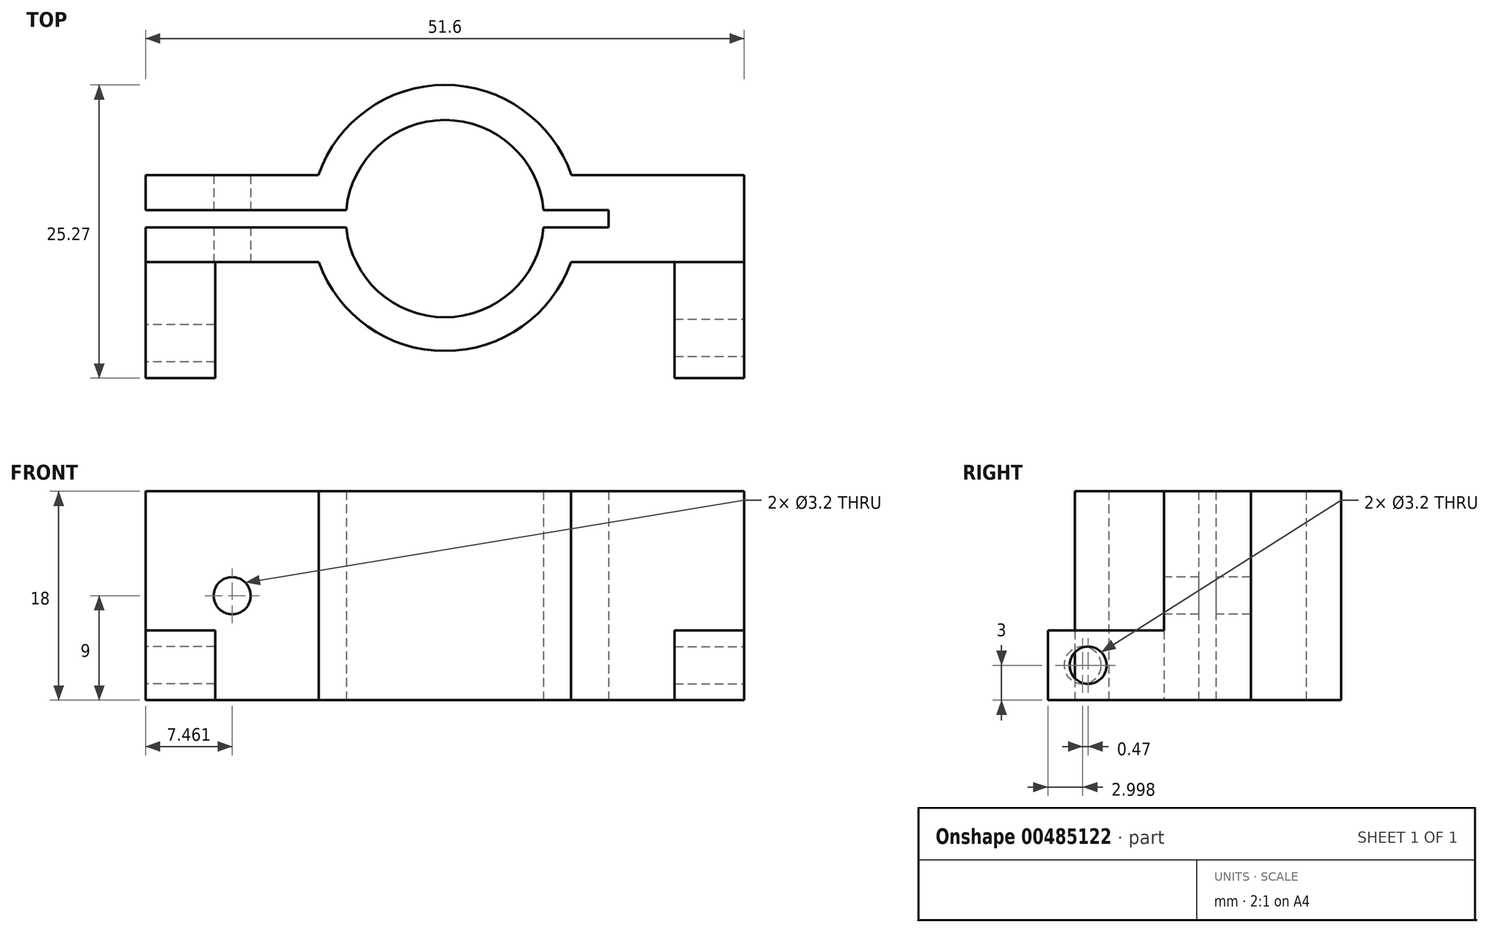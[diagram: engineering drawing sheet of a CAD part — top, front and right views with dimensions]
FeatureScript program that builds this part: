
annotation { "Feature Type Name" : "Feature", "Feature Type Description" : "" }
export const myFeature = defineFeature(function(context is Context, id is Id, definition is map)
    precondition{}
    {
        {
            var Q0;
            Q0=qCreatedBy(makeId("Top.planeOp"),FACE);
            var sketch = newSketch(context, id + "F0", { "sketchPlane" : qUnion([Q0])});
            skLineSegment(sketch, "E0.bottom", {"start": v(-14.3, 13.28) * mm, "end": v(3, 13.28) * mm, "construction": true});
            skLineSegment(sketch, "E0.left", {"start": v(-14.3, 13.28) * mm, "end": v(-14.3, 10.28) * mm, "construction": true});
            skLineSegment(sketch, "E0.right", {"start": v(3, 13.28) * mm, "end": v(3, 10.28) * mm, "construction": true});
            skLineSegment(sketch, "E1.bottom", {"start": v(20, 10.28) * mm, "end": v(37.3, 10.28) * mm, "construction": true});
            skLineSegment(sketch, "E1.top", {"start": v(20, 13.28) * mm, "end": v(33.6, 13.28) * mm, "construction": true});
            skLineSegment(sketch, "E1.left", {"start": v(20, 10.28) * mm, "end": v(20, 13.28) * mm, "construction": true});
            skLineSegment(sketch, "E2", {"start": v(0, 13.28) * mm, "end": v(0, 10.28) * mm, "construction": true});
            skLineSegment(sketch, "E3", {"start": v(23, 13.28) * mm, "end": v(23, 10.28) * mm, "construction": true});
            skLineSegment(sketch, "E4", {"start": v(-14.3, 13.28) * mm, "end": v(3, 13.28) * mm});
            skLineSegment(sketch, "E5", {"start": v(20, 13.28) * mm, "end": v(23, 13.28) * mm});
            skLineSegment(sketch, "E6", {"start": v(20, 13.28) * mm, "end": v(20, 10.28) * mm});
            skLineSegment(sketch, "E7", {"start": v(3, 13.28) * mm, "end": v(3, 10.28) * mm});
            skLineSegment(sketch, "E8", {"start": v(-14.3, 13.28) * mm, "end": v(-14.3, 10.28) * mm});
            skLineSegment(sketch, "E9", {"start": v(37.3, 10.28) * mm, "end": v(23, 10.28) * mm});
            skLineSegment(sketch, "E10.bottom", {"start": v(33.6, 14.78) * mm, "end": v(20, 14.78) * mm, "construction": true});
            skLineSegment(sketch, "E10.top", {"start": v(37.3, 17.78) * mm, "end": v(20, 17.78) * mm, "construction": true});
            skLineSegment(sketch, "E10.right", {"start": v(20, 14.78) * mm, "end": v(20, 17.78) * mm, "construction": true});
            skLineSegment(sketch, "E11", {"start": v(23, 13.28) * mm, "end": v(23, 17.78) * mm, "construction": true});
            skLineSegment(sketch, "E12.bottom", {"start": v(3, 14.78) * mm, "end": v(-14.3, 14.78) * mm, "construction": true});
            skLineSegment(sketch, "E12.top", {"start": v(3, 17.78) * mm, "end": v(-14.3, 17.78) * mm, "construction": true});
            skLineSegment(sketch, "E12.left", {"start": v(3, 14.78) * mm, "end": v(3, 17.78) * mm, "construction": true});
            skLineSegment(sketch, "E12.right", {"start": v(-14.3, 14.78) * mm, "end": v(-14.3, 17.78) * mm, "construction": true});
            skLineSegment(sketch, "E13", {"start": v(20, 14.78) * mm, "end": v(20, 13.28) * mm, "construction": true});
            skPoint(sketch, "E14", {"position": v(20, 14.03) * mm});
            skLineSegment(sketch, "E15", {"start": v(3, 14.78) * mm, "end": v(3, 13.28) * mm, "construction": true});
            skLineSegment(sketch, "E16", {"start": v(3, 14.03) * mm, "end": v(20, 14.03) * mm, "construction": true});
            skPoint(sketch, "E17", {"position": v(11.5, 14.03) * mm});
            skArc(sketch, "E18", {"start": v(20, 14.78) * mm, "mid": v(11.5, 22.54) * mm, "end": v(3, 14.78) * mm, "construction": true});
            skArc(sketch, "E19", {"start": v(3, 13.28) * mm, "mid": v(11.5, 5.48) * mm, "end": v(20, 13.28) * mm, "construction": true});
            skArc(sketch, "E20", {"start": v(0, 13.28) * mm, "mid": v(11.5, 2.57) * mm, "end": v(23, 13.28) * mm, "construction": true});
            skArc(sketch, "E21", {"start": v(23, 14.78) * mm, "mid": v(11.5, 25.58) * mm, "end": v(0, 14.78) * mm, "construction": true});
            skLineSegment(sketch, "E22", {"start": v(25.6, 14.78) * mm, "end": v(25.6, 13.28) * mm, "construction": true});
            skLineSegment(sketch, "E23", {"start": v(-14.3, 10.28) * mm, "end": v(3, 10.28) * mm, "construction": true});
            skLineSegment(sketch, "E24", {"start": v(-14.3, 10.28) * mm, "end": v(0.62, 10.28) * mm});
            skLineSegment(sketch, "E25", {"start": v(-14.3, 14.78) * mm, "end": v(3, 14.78) * mm});
            skLineSegment(sketch, "E26", {"start": v(-14.3, 14.78) * mm, "end": v(-14.3, 17.78) * mm});
            skLineSegment(sketch, "E27", {"start": v(-14.3, 17.78) * mm, "end": v(0.6, 17.78) * mm});
            skLineSegment(sketch, "E28", {"start": v(20, 13.28) * mm, "end": v(25.6, 13.28) * mm});
            skLineSegment(sketch, "E29", {"start": v(25.6, 13.28) * mm, "end": v(25.6, 14.78) * mm});
            skLineSegment(sketch, "E30", {"start": v(25.6, 14.78) * mm, "end": v(20, 14.78) * mm});
            skLineSegment(sketch, "E31", {"start": v(37.3, 17.78) * mm, "end": v(22.4, 17.78) * mm});
            skArc(sketch, "E32", {"start": v(20, 14.78) * mm, "mid": v(11.5, 22.53) * mm, "end": v(3, 14.78) * mm});
            skArc(sketch, "E33", {"start": v(3, 13.28) * mm, "mid": v(11.5, 5.52) * mm, "end": v(20, 13.28) * mm});
            skArc(sketch, "E34", {"start": v(0.62, 10.28) * mm, "mid": v(11.5, 2.62) * mm, "end": v(22.38, 10.28) * mm});
            skArc(sketch, "E35", {"start": v(22.4, 17.78) * mm, "mid": v(11.5, 25.55) * mm, "end": v(0.6, 17.78) * mm});
            skLineSegment(sketch, "E36", {"start": v(37.3, 17.78) * mm, "end": v(37.3, 10.28) * mm});
            skLineSegment(sketch, "E37", {"start": v(23, 10.28) * mm, "end": v(22.38, 10.28) * mm});
            skSolve(sketch);
        }
        {
            var Q0;
            Q0 = qSketchRegion(id + "F0", true);
            extrude(context, id + "F1", {"entities" : qUnion([Q0]), "depth" : 18 * mm, "offsetDistance" : 25 * mm});
        }
        {
            var Q0;
            Q0=makeQuery(id+"F1.opExtrude","SWEPT_FACE",FACE,{"disambiguationData":[OSD([sQuery(id+"F0.wireOp",EDGE,"E24")])]});
            var sketch = newSketch(context, id + "F2", { "sketchPlane" : qUnion([Q0])});
            skLineSegment(sketch, "E38.bottom", {"start": v(-14.3, 18) * mm, "end": v(0.62, 18) * mm, "construction": true});
            skLineSegment(sketch, "E38.top", {"start": v(-14.3, 0) * mm, "end": v(0.62, 0) * mm, "construction": true});
            skLineSegment(sketch, "E38.left", {"start": v(-14.3, 18) * mm, "end": v(-14.3, 0) * mm, "construction": true});
            skLineSegment(sketch, "E38.right", {"start": v(0.62, 18) * mm, "end": v(0.62, 0) * mm, "construction": true});
            skLineSegment(sketch, "E39", {"start": v(-6.84, 18) * mm, "end": v(-6.84, 0) * mm, "construction": true});
            skLineSegment(sketch, "E40", {"start": v(-14.3, 9) * mm, "end": v(0.62, 9) * mm, "construction": true});
            skCircle(sketch, "E41", {"center": v(-6.84, 9) * mm, "radius": 0.84 * mm, "construction": true});
            skSolve(sketch);
        }
        {
            var Q0;
            Q0=sQuery(id+"F2.wireOp",VERTEX,"E41.center");
            var Q1;
            Q1=makeQuery(id+"F1.opExtrude","SWEPT_BODY",BODY,{"disambiguationData":[OSD([sQuery(id+"F0.wireOp",EDGE,"E4"),sQuery(id+"F0.wireOp",EDGE,"E8"),sQuery(id+"F0.wireOp",EDGE,"E9"),sQuery(id+"F0.wireOp",EDGE,"E24"),sQuery(id+"F0.wireOp",EDGE,"E25"),sQuery(id+"F0.wireOp",EDGE,"E26"),sQuery(id+"F0.wireOp",EDGE,"E27"),sQuery(id+"F0.wireOp",EDGE,"E28"),sQuery(id+"F0.wireOp",EDGE,"E29"),sQuery(id+"F0.wireOp",EDGE,"E30"),sQuery(id+"F0.wireOp",EDGE,"E31"),sQuery(id+"F0.wireOp",EDGE,"E32"),sQuery(id+"F0.wireOp",EDGE,"E33"),sQuery(id+"F0.wireOp",EDGE,"E34"),sQuery(id+"F0.wireOp",EDGE,"E35"),sQuery(id+"F0.wireOp",EDGE,"E36"),sQuery(id+"F0.wireOp",EDGE,"E37")])]});
            hole(context, id + "F3", {"style" : HoleStyle.SIMPLE, "endStyle" : HoleEndStyle.BLIND, "holeDiameter" : 3.2 * mm, "holeDepth" : 15 * mm, "isTappedThrough" : true, "tappedDepth" : 12 * mm, "tapClearance" : 3, "locations" : qUnion([Q0]), "scope" : qUnion([Q1])});
        }
        {
            var Q0;
            Q0=makeQuery(id+"F1.opExtrude","SWEPT_FACE",FACE,{"disambiguationData":[OSD([sQuery(id+"F0.wireOp",EDGE,"E9"),sQuery(id+"F0.wireOp",EDGE,"E37")])]});
            var sketch = newSketch(context, id + "F4", { "sketchPlane" : qUnion([Q0])});
            skLineSegment(sketch, "E42.bottom", {"start": v(22.38, 0) * mm, "end": v(37.3, 0) * mm, "construction": true});
            skLineSegment(sketch, "E42.top", {"start": v(22.38, 6) * mm, "end": v(37.3, 6) * mm, "construction": true});
            skLineSegment(sketch, "E42.left", {"start": v(22.38, 0) * mm, "end": v(22.38, 6) * mm, "construction": true});
            skLineSegment(sketch, "E42.right", {"start": v(37.3, 0) * mm, "end": v(37.3, 6) * mm, "construction": true});
            skLineSegment(sketch, "E43", {"start": v(31.3, 6) * mm, "end": v(31.3, 0) * mm, "construction": true});
            skLineSegment(sketch, "E44.bottom", {"start": v(31.3, 6) * mm, "end": v(37.3, 6) * mm});
            skLineSegment(sketch, "E44.top", {"start": v(31.3, 0) * mm, "end": v(37.3, 0) * mm});
            skLineSegment(sketch, "E44.left", {"start": v(31.3, 6) * mm, "end": v(31.3, 0) * mm});
            skLineSegment(sketch, "E44.right", {"start": v(37.3, 6) * mm, "end": v(37.3, 0) * mm});
            skSolve(sketch);
        }
        {
            var Q0;
            Q0=makeQuery(id+"F4.imprint","IMPRINT",FACE,{"disambiguationData":[TD([[makeQuery(id+"F4.imprint","IMPRINT",EDGE,{"derivedFrom":sQuery(id+"F4.wireOp",EDGE,"E44.bottom")}),-1.0]])]});
            extrude(context, id + "F5", {"entities" : qUnion([Q0]), "operationType" : NewBodyOperationType.ADD, "depth" : 10 * mm, "offsetDistance" : 25 * mm});
        }
        {
            var Q0;
            Q0=makeQuery(id+"F1.opExtrude","SWEPT_FACE",FACE,{"disambiguationData":[OSD([sQuery(id+"F0.wireOp",EDGE,"E24")])]});
            var sketch = newSketch(context, id + "F6", { "sketchPlane" : qUnion([Q0])});
            skLineSegment(sketch, "E45.bottom", {"start": v(-14.3, 0) * mm, "end": v(0.62, 0) * mm, "construction": true});
            skLineSegment(sketch, "E45.top", {"start": v(-14.3, 6) * mm, "end": v(0.62, 6) * mm, "construction": true});
            skLineSegment(sketch, "E45.left", {"start": v(-14.3, 0) * mm, "end": v(-14.3, 6) * mm, "construction": true});
            skLineSegment(sketch, "E45.right", {"start": v(0.62, 0) * mm, "end": v(0.62, 6) * mm, "construction": true});
            skLineSegment(sketch, "E46", {"start": v(-8.3, 6) * mm, "end": v(-8.3, 0) * mm, "construction": true});
            skLineSegment(sketch, "E47.bottom", {"start": v(-14.3, 6) * mm, "end": v(-8.3, 6) * mm});
            skLineSegment(sketch, "E47.top", {"start": v(-14.3, 0) * mm, "end": v(-8.3, 0) * mm});
            skLineSegment(sketch, "E47.left", {"start": v(-14.3, 6) * mm, "end": v(-14.3, 0) * mm});
            skLineSegment(sketch, "E47.right", {"start": v(-8.3, 6) * mm, "end": v(-8.3, 0) * mm});
            skSolve(sketch);
        }
        {
            var Q0;
            Q0=makeQuery(id+"F6.imprint","IMPRINT",FACE,{"disambiguationData":[TD([[makeQuery(id+"F6.imprint","IMPRINT",EDGE,{"derivedFrom":sQuery(id+"F6.wireOp",EDGE,"E47.bottom")}),-1.0]])]});
            extrude(context, id + "F7", {"entities" : qUnion([Q0]), "operationType" : NewBodyOperationType.ADD, "depth" : 10 * mm, "offsetDistance" : 25 * mm});
        }
        {
            var Q0;
            Q0=makeQuery(id+"F5.boolean.opBoolean","MERGE",FACE,{"derivedFrom":[makeQuery(id+"F1.opExtrude","SWEPT_FACE",FACE,{"disambiguationData":[OSD([sQuery(id+"F0.wireOp",EDGE,"E36")])]}),makeQuery(id+"F5.opExtrude","SWEPT_FACE",FACE,{"disambiguationData":[OSD([sQuery(id+"F4.wireOp",EDGE,"E44.right")])]})]});
            var sketch = newSketch(context, id + "F8", { "sketchPlane" : qUnion([Q0])});
            skLineSegment(sketch, "E48.bottom", {"start": v(0.28, 6) * mm, "end": v(7.22, 6) * mm, "construction": true});
            skLineSegment(sketch, "E48.top", {"start": v(0.28, 0) * mm, "end": v(7.22, 0) * mm, "construction": true});
            skLineSegment(sketch, "E48.left", {"start": v(0.28, 6) * mm, "end": v(0.28, 0) * mm, "construction": true});
            skLineSegment(sketch, "E48.right", {"start": v(7.22, 6) * mm, "end": v(7.22, 0) * mm, "construction": true});
            skLineSegment(sketch, "E49", {"start": v(3.75, 6) * mm, "end": v(3.75, 0) * mm, "construction": true});
            skCircle(sketch, "E50", {"center": v(3.75, 3) * mm, "radius": 0.47 * mm, "construction": true});
            skSolve(sketch);
        }
        {
            var Q0;
            Q0=sQuery(id+"F8.wireOp",VERTEX,"E50.center");
            var Q1;
            Q1=makeQuery(id+"F1.opExtrude","SWEPT_BODY",BODY,{"disambiguationData":[OSD([sQuery(id+"F0.wireOp",EDGE,"E4"),sQuery(id+"F0.wireOp",EDGE,"E8"),sQuery(id+"F0.wireOp",EDGE,"E9"),sQuery(id+"F0.wireOp",EDGE,"E24"),sQuery(id+"F0.wireOp",EDGE,"E25"),sQuery(id+"F0.wireOp",EDGE,"E26"),sQuery(id+"F0.wireOp",EDGE,"E27"),sQuery(id+"F0.wireOp",EDGE,"E28"),sQuery(id+"F0.wireOp",EDGE,"E29"),sQuery(id+"F0.wireOp",EDGE,"E30"),sQuery(id+"F0.wireOp",EDGE,"E31"),sQuery(id+"F0.wireOp",EDGE,"E32"),sQuery(id+"F0.wireOp",EDGE,"E33"),sQuery(id+"F0.wireOp",EDGE,"E34"),sQuery(id+"F0.wireOp",EDGE,"E35"),sQuery(id+"F0.wireOp",EDGE,"E36"),sQuery(id+"F0.wireOp",EDGE,"E37")])]});
            hole(context, id + "F9", {"style" : HoleStyle.SIMPLE, "endStyle" : HoleEndStyle.BLIND, "holeDiameter" : 3.2 * mm, "holeDepth" : 6 * mm, "isTappedThrough" : true, "tappedDepth" : 12 * mm, "tapClearance" : 3, "locations" : qUnion([Q0]), "scope" : qUnion([Q1])});
        }
        {
            var Q0;
            Q0=makeQuery(id+"F7.boolean.opBoolean","MERGE",FACE,{"derivedFrom":[makeQuery(id+"F1.opExtrude","SWEPT_FACE",FACE,{"disambiguationData":[OSD([sQuery(id+"F0.wireOp",EDGE,"E8")])]}),makeQuery(id+"F7.opExtrude","SWEPT_FACE",FACE,{"disambiguationData":[OSD([sQuery(id+"F6.wireOp",EDGE,"E47.left")])]})]});
            var sketch = newSketch(context, id + "F10", { "sketchPlane" : qUnion([Q0])});
            skLineSegment(sketch, "E51.bottom", {"start": v(-0.28, 6) * mm, "end": v(-6.28, 6) * mm, "construction": true});
            skLineSegment(sketch, "E51.top", {"start": v(-0.28, 0) * mm, "end": v(-6.28, 0) * mm, "construction": true});
            skLineSegment(sketch, "E51.left", {"start": v(-0.28, 6) * mm, "end": v(-0.28, 0) * mm, "construction": true});
            skLineSegment(sketch, "E51.right", {"start": v(-6.28, 6) * mm, "end": v(-6.28, 0) * mm, "construction": true});
            skLineSegment(sketch, "E52", {"start": v(-3.28, 6) * mm, "end": v(-3.28, 0) * mm, "construction": true});
            skCircle(sketch, "E53", {"center": v(-3.28, 3) * mm, "radius": 0.68 * mm, "construction": true});
            skSolve(sketch);
        }
        {
            var Q0;
            Q0=sQuery(id+"F10.wireOp",VERTEX,"E53.center");
            var Q1;
            Q1=makeQuery(id+"F1.opExtrude","SWEPT_BODY",BODY,{"disambiguationData":[OSD([sQuery(id+"F0.wireOp",EDGE,"E4"),sQuery(id+"F0.wireOp",EDGE,"E8"),sQuery(id+"F0.wireOp",EDGE,"E9"),sQuery(id+"F0.wireOp",EDGE,"E24"),sQuery(id+"F0.wireOp",EDGE,"E25"),sQuery(id+"F0.wireOp",EDGE,"E26"),sQuery(id+"F0.wireOp",EDGE,"E27"),sQuery(id+"F0.wireOp",EDGE,"E28"),sQuery(id+"F0.wireOp",EDGE,"E29"),sQuery(id+"F0.wireOp",EDGE,"E30"),sQuery(id+"F0.wireOp",EDGE,"E31"),sQuery(id+"F0.wireOp",EDGE,"E32"),sQuery(id+"F0.wireOp",EDGE,"E33"),sQuery(id+"F0.wireOp",EDGE,"E34"),sQuery(id+"F0.wireOp",EDGE,"E35"),sQuery(id+"F0.wireOp",EDGE,"E36"),sQuery(id+"F0.wireOp",EDGE,"E37")])]});
            hole(context, id + "F11", {"style" : HoleStyle.SIMPLE, "endStyle" : HoleEndStyle.BLIND, "holeDiameter" : 3.2 * mm, "holeDepth" : 6 * mm, "isTappedThrough" : true, "tappedDepth" : 12 * mm, "tapClearance" : 3, "locations" : qUnion([Q0]), "scope" : qUnion([Q1])});
        }
    });
